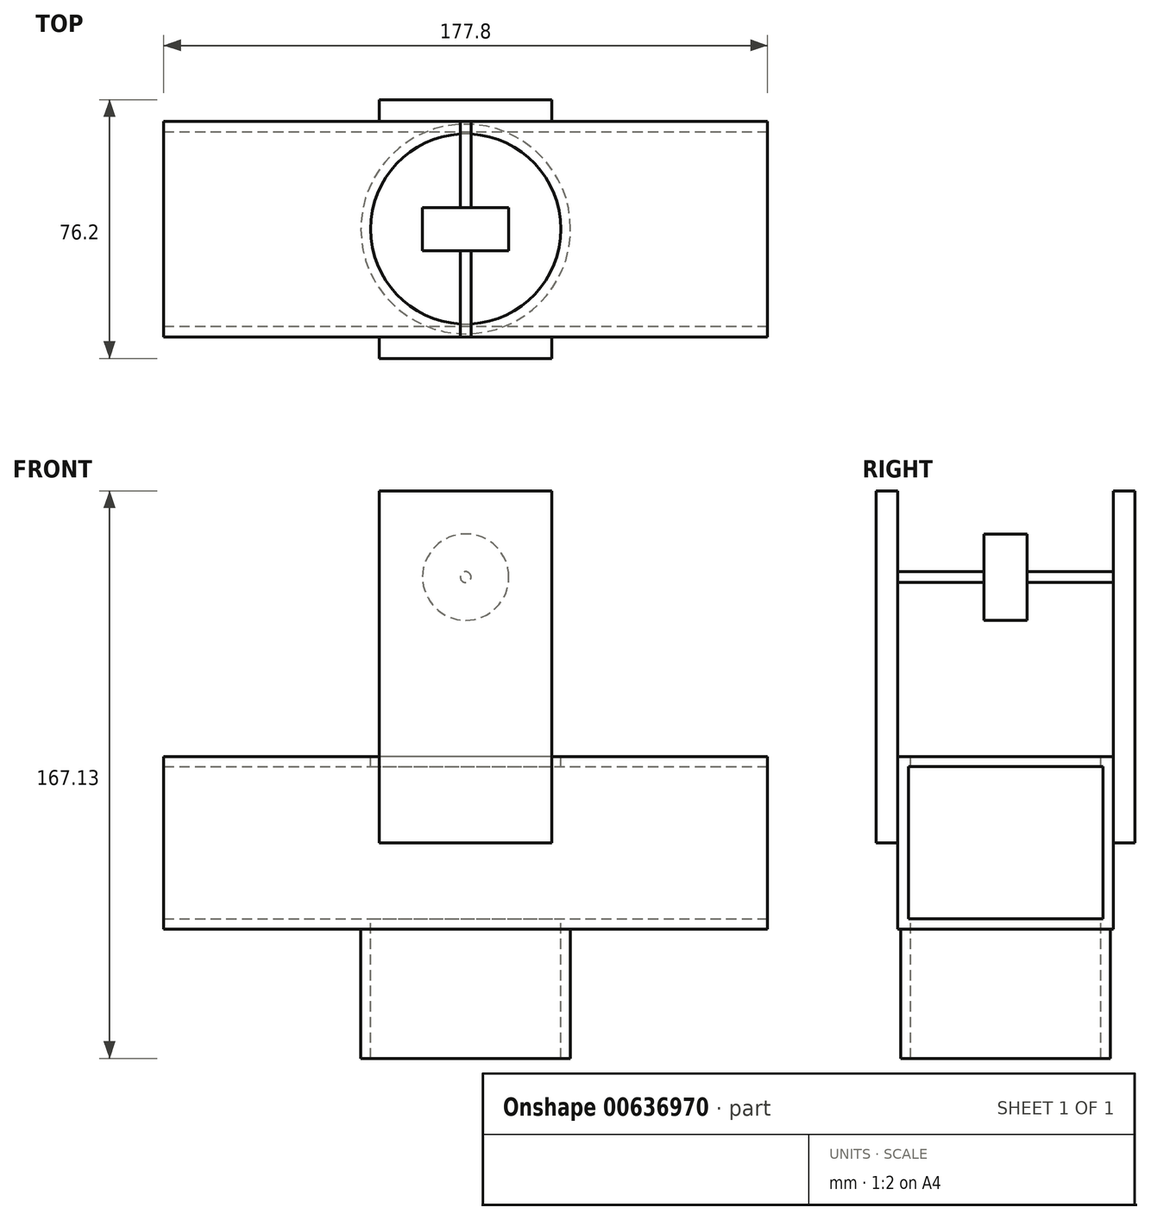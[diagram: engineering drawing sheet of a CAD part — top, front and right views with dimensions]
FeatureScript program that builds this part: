
annotation { "Feature Type Name" : "Feature", "Feature Type Description" : "" }
export const myFeature = defineFeature(function(context is Context, id is Id, definition is map)
    precondition{}
    {
        {
            var Q0;
            Q0=qCreatedBy(makeId("Front.planeOp"),FACE);
            var sketch = newSketch(context, id + "F0", { "sketchPlane" : qUnion([Q0])});
            skLineSegment(sketch, "E0", {"start": v(0, 0) * mm, "end": v(177.8, 0) * mm});
            skLineSegment(sketch, "E1", {"start": v(177.8, 0) * mm, "end": v(177.8, 50.8) * mm});
            skLineSegment(sketch, "E2", {"start": v(177.8, 50.8) * mm, "end": v(0, 50.8) * mm});
            skLineSegment(sketch, "E3", {"start": v(0, 50.8) * mm, "end": v(0, 0) * mm});
            skSolve(sketch);
        }
        {
            var Q0;
            Q0=makeQuery(id+"F0.imprint","IMPRINT",FACE,{"disambiguationData":[TD([[makeQuery(id+"F0.imprint","IMPRINT",EDGE,{"derivedFrom":sQuery(id+"F0.wireOp",EDGE,"E0")}),1.0]])]});
            extrude(context, id + "F1", {"entities" : qUnion([Q0]), "depth" : 63.5 * mm, "offsetDistance" : 25.4 * mm});
        }
        {
            var Q0;
            Q0=makeQuery(id+"F1.opExtrude","CAP_FACE",FACE,{"disambiguationData":[OSD([sQuery(id+"F0.wireOp",EDGE,"E0"),sQuery(id+"F0.wireOp",EDGE,"E1"),sQuery(id+"F0.wireOp",EDGE,"E2"),sQuery(id+"F0.wireOp",EDGE,"E3")])],"isStart":false});
            var sketch = newSketch(context, id + "F2", { "sketchPlane" : qUnion([Q0])});
            skPoint(sketch, "E4.endSnap0", {"position": v(0, 25.4) * mm});
            skLineSegment(sketch, "E5.bottom", {"start": v(88.9, 25.4) * mm, "end": v(88.9, 25.4) * mm});
            skLineSegment(sketch, "E6", {"start": v(88.9, 25.4) * mm, "end": v(63.5, 25.4) * mm});
            skLineSegment(sketch, "E7", {"start": v(88.9, 25.4) * mm, "end": v(114.3, 25.4) * mm});
            skLineSegment(sketch, "E8", {"start": v(114.3, 25.4) * mm, "end": v(114.3, 129.03) * mm});
            skLineSegment(sketch, "E9", {"start": v(114.3, 129.03) * mm, "end": v(63.5, 129.03) * mm});
            skLineSegment(sketch, "E10", {"start": v(63.5, 129.03) * mm, "end": v(63.5, 25.4) * mm});
            skSolve(sketch);
        }
        {
            var Q0;
            {var subQ0=sQuery(id+"F2.wireOp",EDGE,"E9");Q0=makeQuery(id+"F2.imprint","IMPRINT",FACE,{"disambiguationData":[TD([[makeQuery(id+"F2.imprint","IMPRINT",EDGE,{"derivedFrom":subQ0}),1.0]])]});}
            var Q1;
            {var subQ5=sQuery(id+"F2.wireOp",EDGE,"E6");Q1=makeQuery(id+"F2.imprint","IMPRINT",FACE,{"disambiguationData":[TD([[makeQuery(id+"F2.imprint","IMPRINT",EDGE,{"derivedFrom":subQ5}),-1.0]])]});}
            extrude(context, id + "F3", {"entities" : qUnion([Q0, Q1]), "operationType" : NewBodyOperationType.ADD, "depth" : 6.35 * mm, "offsetDistance" : 25.4 * mm});
        }
        {
            var Q0;
            Q0=makeQuery(id+"F1.opExtrude","CAP_FACE",FACE,{"disambiguationData":[OSD([sQuery(id+"F0.wireOp",EDGE,"E0"),sQuery(id+"F0.wireOp",EDGE,"E1"),sQuery(id+"F0.wireOp",EDGE,"E2"),sQuery(id+"F0.wireOp",EDGE,"E3")])],"isStart":true});
            var sketch = newSketch(context, id + "F4", { "sketchPlane" : qUnion([Q0])});
            skLineSegment(sketch, "E11.0", {"start": v(-114.3, 25.4) * mm, "end": v(-63.5, 25.4) * mm});
            skLineSegment(sketch, "E12.0", {"start": v(-114.3, 25.4) * mm, "end": v(-114.3, 50.8) * mm});
            skPoint(sketch, "E13.0", {"position": v(-63.5, 38.1) * mm});
            skLineSegment(sketch, "E14.0", {"start": v(-63.5, 129.03) * mm, "end": v(-63.5, 50.8) * mm});
            skLineSegment(sketch, "E15.0", {"start": v(-114.3, 50.8) * mm, "end": v(-114.3, 129.03) * mm});
            skLineSegment(sketch, "E16.0", {"start": v(-114.3, 129.03) * mm, "end": v(-63.5, 129.03) * mm});
            skLineSegment(sketch, "E17", {"start": v(-63.5, 25.4) * mm, "end": v(-63.5, 50.8) * mm});
            skSolve(sketch);
        }
        {
            var Q0;
            {var subQ0=sQuery(id+"F4.wireOp",EDGE,"E14.0");Q0=makeQuery(id+"F4.imprint","IMPRINT",FACE,{"disambiguationData":[TD([[makeQuery(id+"F4.imprint","IMPRINT",EDGE,{"derivedFrom":subQ0}),-1.0]])]});}
            var Q1;
            Q1=makeQuery(id+"F4.imprint","IMPRINT",FACE,{"disambiguationData":[TD([[makeQuery(id+"F4.imprint","IMPRINT",EDGE,{"derivedFrom":sQuery(id+"F4.wireOp",EDGE,"E11.0")}),1.0]])]});
            extrude(context, id + "F5", {"entities" : qUnion([Q0, Q1]), "operationType" : NewBodyOperationType.ADD, "depth" : 6.35 * mm, "offsetDistance" : 25.4 * mm});
        }
        {
            var Q0;
            Q0=makeQuery(id+"F1.opExtrude","SWEPT_FACE",FACE,{"disambiguationData":[OSD([sQuery(id+"F0.wireOp",EDGE,"E1")])]});
            var sketch = newSketch(context, id + "F6", { "sketchPlane" : qUnion([Q0])});
            skLineSegment(sketch, "E18.bottom", {"start": v(-60.37, 47.8) * mm, "end": v(-3.13, 47.8) * mm});
            skLineSegment(sketch, "E18.top", {"start": v(-60.37, 3) * mm, "end": v(-3.13, 3) * mm});
            skLineSegment(sketch, "E18.left", {"start": v(-60.37, 47.8) * mm, "end": v(-60.37, 3) * mm});
            skLineSegment(sketch, "E18.right", {"start": v(-3.13, 47.8) * mm, "end": v(-3.13, 3) * mm});
            skPoint(sketch, "E18.middle", {"position": v(-31.75, 25.4) * mm});
            skPoint(sketch, "E18.middle.positionSnap0", {"position": v(0, 25.4) * mm});
            skPoint(sketch, "E18.middle.positionSnap1", {"position": v(-31.75, 0) * mm});
            skPoint(sketch, "E18.centerSnap0", {"position": v(0, 25.4) * mm});
            skPoint(sketch, "E18.centerSnap1", {"position": v(-31.75, 0) * mm});
            skSolve(sketch);
        }
        {
            var Q0;
            Q0=makeQuery(id+"F6.imprint","IMPRINT",FACE,{"disambiguationData":[TD([[makeQuery(id+"F6.imprint","IMPRINT",EDGE,{"derivedFrom":sQuery(id+"F6.wireOp",EDGE,"E18.bottom")}),-1.0]])]});
            extrude(context, id + "F7", {"entities" : qUnion([Q0]), "operationType" : NewBodyOperationType.REMOVE, "endBound" : BoundingType.UP_TO_NEXT, "oppositeDirection" : true, "depth" : 25.4 * mm, "offsetDistance" : 25.4 * mm});
        }
        {
            var Q0;
            Q0=makeQuery(id+"F1.opExtrude","SWEPT_FACE",FACE,{"disambiguationData":[OSD([sQuery(id+"F0.wireOp",EDGE,"E2")])]});
            var sketch = newSketch(context, id + "F8", { "sketchPlane" : qUnion([Q0])});
            skCircle(sketch, "E19", {"center": v(88.9, -31.75) * mm, "radius": 28 * mm});
            skPoint(sketch, "E19.centerSnap0", {"position": v(0, -31.75) * mm});
            skPoint(sketch, "E19.centerSnap1", {"position": v(88.9, 0) * mm});
            skSolve(sketch);
        }
        {
            var Q0;
            Q0=makeQuery(id+"F8.imprint","IMPRINT",FACE,{"disambiguationData":[TD([[makeQuery(id+"F8.imprint","IMPRINT",EDGE,{"derivedFrom":sQuery(id+"F8.wireOp",EDGE,"E19")}),1.0]])]});
            extrude(context, id + "F9", {"entities" : qUnion([Q0]), "operationType" : NewBodyOperationType.REMOVE, "endBound" : BoundingType.THROUGH_ALL, "oppositeDirection" : true, "depth" : 25.4 * mm, "offsetDistance" : 25.4 * mm});
        }
        {
            var Q0;
            Q0=makeQuery(id+"F1.opExtrude","SWEPT_FACE",FACE,{"disambiguationData":[OSD([sQuery(id+"F0.wireOp",EDGE,"E0")])]});
            var sketch = newSketch(context, id + "F10", { "sketchPlane" : qUnion([Q0])});
            skCircle(sketch, "E20", {"center": v(88.9, 31.75) * mm, "radius": 30.86 * mm});
            skSolve(sketch);
        }
        {
            var Q0;
            Q0=makeQuery(id+"F10.imprint","IMPRINT",FACE,{"disambiguationData":[TD([[makeQuery(id+"F10.imprint","IMPRINT",EDGE,{"derivedFrom":sQuery(id+"F10.wireOp",EDGE,"E20")}),1.0]])]});
            extrude(context, id + "F11", {"entities" : qUnion([Q0]), "operationType" : NewBodyOperationType.ADD, "depth" : 38.1 * mm, "offsetDistance" : 25.4 * mm});
        }
        {
            var Q0;
            Q0=makeQuery(id+"F1.opExtrude","SWEPT_FACE",FACE,{"disambiguationData":[OSD([sQuery(id+"F0.wireOp",EDGE,"E2")])]});
            var sketch = newSketch(context, id + "F12", { "sketchPlane" : qUnion([Q0])});
            skLineSegment(sketch, "E21", {"start": v(177.8, -31.75) * mm, "end": v(116.9, -31.75) * mm});
            skSolve(sketch);
        }
        {
            var Q0;
            Q0=qCreatedBy(makeId("Front.planeOp"),FACE);
            var Q1;
            Q1=sQuery(id+"F12.wireOp",VERTEX,"E21.end");
            cPlane(context, id + "F13", {"entities" : qUnion([Q0, Q1]), "cplaneType" : CPlaneType.PLANE_POINT, "offset" : 25.4 * mm, "width" : 152.4 * mm, "height" : 152.4 * mm});
        }
        {
            var Q0;
            Q0=qCreatedBy(id+"F13.planeOp",FACE);
            var sketch = newSketch(context, id + "F14", { "sketchPlane" : qUnion([Q0])});
            skLineSegment(sketch, "E22.0.0", {"start": v(63.5, 50.8) * mm, "end": v(114.3, 50.8) * mm});
            skLineSegment(sketch, "E22.0.1", {"start": v(114.3, 50.8) * mm, "end": v(114.3, 129.03) * mm});
            skLineSegment(sketch, "E22.0.2", {"start": v(114.3, 129.03) * mm, "end": v(63.5, 129.03) * mm});
            skLineSegment(sketch, "E22.0.3", {"start": v(63.5, 129.03) * mm, "end": v(63.5, 50.8) * mm});
            skCircle(sketch, "E23", {"center": v(88.9, 103.63) * mm, "radius": 12.7 * mm});
            skSolve(sketch);
        }
        {
            var Q0;
            Q0=makeQuery(id+"F14.imprint","IMPRINT",FACE,{"disambiguationData":[TD([[makeQuery(id+"F14.imprint","IMPRINT",EDGE,{"derivedFrom":sQuery(id+"F14.wireOp",EDGE,"E23")}),1.0]])]});
            extrude(context, id + "F15", {"entities" : qUnion([Q0]), "endBound" : BoundingType.SYMMETRIC, "depth" : 12.7 * mm, "offsetDistance" : 25.4 * mm});
        }
        {
            var Q0;
            Q0=makeQuery(id+"F15.opExtrude","CAP_FACE",FACE,{"disambiguationData":[OSD([sQuery(id+"F14.wireOp",EDGE,"E23")])],"isStart":true});
            var sketch = newSketch(context, id + "F16", { "sketchPlane" : qUnion([Q0])});
            skCircle(sketch, "E24", {"center": v(-88.9, 103.63) * mm, "radius": 1.59 * mm});
            skSolve(sketch);
        }
        {
            var Q0;
            Q0 = qSketchRegion(id + "F16", true);
            extrude(context, id + "F17", {"entities" : qUnion([Q0]), "endBound" : BoundingType.UP_TO_NEXT, "depth" : 25.4 * mm, "offsetDistance" : 25.4 * mm});
        }
        {
            var Q0;
            Q0=makeQuery(id+"F15.opExtrude","CAP_FACE",FACE,{"disambiguationData":[OSD([sQuery(id+"F14.wireOp",EDGE,"E23")])],"isStart":false});
            var sketch = newSketch(context, id + "F18", { "sketchPlane" : qUnion([Q0])});
            skCircle(sketch, "E25", {"center": v(88.9, 103.63) * mm, "radius": 1.59 * mm});
            skSolve(sketch);
        }
        {
            var Q0;
            Q0 = qSketchRegion(id + "F18", true);
            extrude(context, id + "F19", {"entities" : qUnion([Q0]), "endBound" : BoundingType.UP_TO_NEXT, "depth" : 25.4 * mm, "offsetDistance" : 25.4 * mm});
        }
    });
